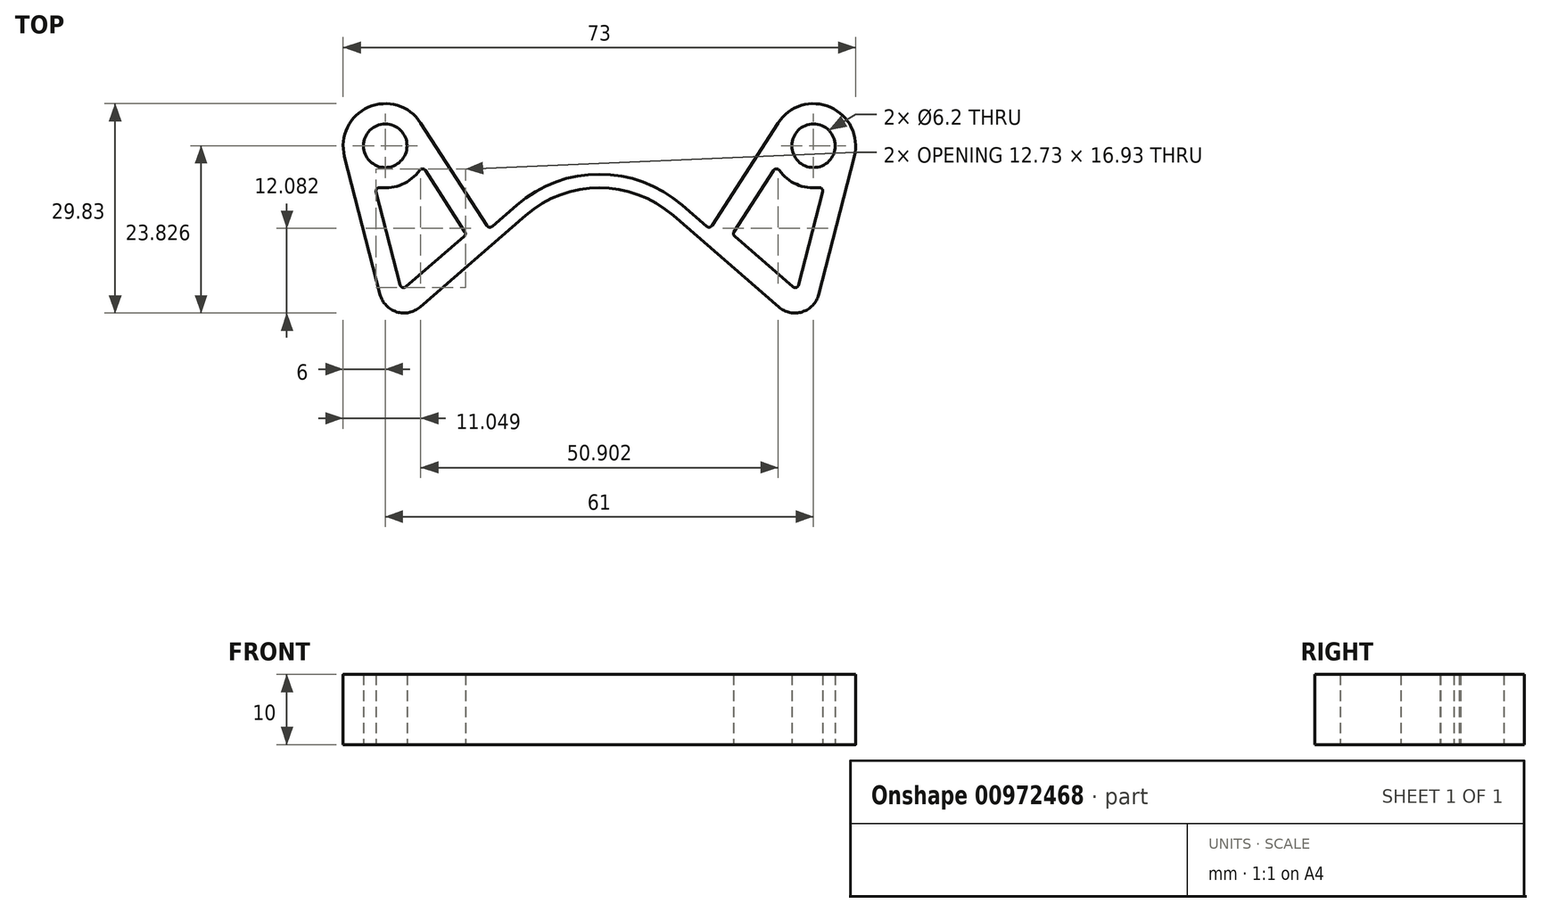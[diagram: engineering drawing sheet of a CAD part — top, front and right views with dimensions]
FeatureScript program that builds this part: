
annotation { "Feature Type Name" : "Feature", "Feature Type Description" : "" }
export const myFeature = defineFeature(function(context is Context, id is Id, definition is map)
    precondition{}
    {
        {
            var Q0;
            Q0=qCreatedBy(makeId("Top.planeOp"),FACE);
            var sketch = newSketch(context, id + "F0", { "sketchPlane" : qUnion([Q0])});
            skCircle(sketch, "E0", {"center": v(30.5, 20.33) * mm, "radius": 3.1 * mm});
            skArc(sketch, "E1", {"start": v(25.62, 16.84) * mm, "mid": v(28.1, 14.83) * mm, "end": v(31.25, 14.37) * mm});
            skArc(sketch, "E2", {"start": v(25.54, -2.64) * mm, "mid": v(28.88, -3.34) * mm, "end": v(31.23, -0.87) * mm});
            skLineSegment(sketch, "E3", {"start": v(31.23, -0.87) * mm, "end": v(36.3, 18.83) * mm});
            skArc(sketch, "E4", {"start": v(10.5, 10.41) * mm, "mid": v(5.6, 13.32) * mm, "end": v(0, 14.34) * mm});
            skLineSegment(sketch, "E5", {"start": v(10.5, 10.41) * mm, "end": v(25.54, -2.64) * mm});
            skArc(sketch, "E6", {"start": v(15.28, 8.85) * mm, "mid": v(15.68, 8.73) * mm, "end": v(16.03, 8.95) * mm});
            skLineSegment(sketch, "E7", {"start": v(16.03, 8.95) * mm, "end": v(25.46, 23.58) * mm});
            skLineSegment(sketch, "E8", {"start": v(19.17, 8.1) * mm, "end": v(24.79, 16.82) * mm});
            skLineSegment(sketch, "E9", {"start": v(19.26, 7.45) * mm, "end": v(27.57, 0.24) * mm});
            skLineSegment(sketch, "E10", {"start": v(31.8, 13.75) * mm, "end": v(28.38, 0.49) * mm});
            skArc(sketch, "E11.trimOffspring", {"start": v(36.3, 18.83) * mm, "mid": v(32.9, 25.82) * mm, "end": v(25.46, 23.58) * mm});
            skPoint(sketch, "E12.visualSharp", {"position": v(18.93, 7.73) * mm});
            skArc(sketch, "E12.filletArc", {"start": v(19.17, 8.1) * mm, "mid": v(19.1, 7.75) * mm, "end": v(19.26, 7.45) * mm});
            skPoint(sketch, "E13.visualSharp", {"position": v(25.22, 17.48) * mm});
            skArc(sketch, "E13.filletArc", {"start": v(25.62, 16.84) * mm, "mid": v(25.2, 17.05) * mm, "end": v(24.79, 16.82) * mm});
            skPoint(sketch, "E14.visualSharp", {"position": v(32, 14.52) * mm});
            skArc(sketch, "E14.filletArc", {"start": v(31.8, 13.75) * mm, "mid": v(31.7, 14.2) * mm, "end": v(31.25, 14.37) * mm});
            skPoint(sketch, "E15.visualSharp", {"position": v(28.18, -0.3) * mm});
            skArc(sketch, "E15.filletArc", {"start": v(27.57, 0.24) * mm, "mid": v(28.04, 0.14) * mm, "end": v(28.38, 0.49) * mm});
            skLineSegment(sketch, "E16", {"start": v(11.78, 11.89) * mm, "end": v(15.28, 8.85) * mm});
            skArc(sketch, "E17.trimOffspring", {"start": v(11.78, 11.89) * mm, "mid": v(6.29, 15.15) * mm, "end": v(0, 16.29) * mm});
            skArc(sketch, "E18.MirrorCS", {"start": v(-27.57, 0.24) * mm, "mid": v(-28.04, 0.14) * mm, "end": v(-28.38, 0.49) * mm});
            skArc(sketch, "E19.MirrorCS", {"start": v(-25.62, 16.84) * mm, "mid": v(-25.2, 17.05) * mm, "end": v(-24.79, 16.82) * mm});
            skArc(sketch, "E20.MirrorCS", {"start": v(-31.8, 13.75) * mm, "mid": v(-31.7, 14.2) * mm, "end": v(-31.25, 14.37) * mm});
            skArc(sketch, "E21.MirrorCS", {"start": v(-19.17, 8.1) * mm, "mid": v(-19.1, 7.75) * mm, "end": v(-19.26, 7.45) * mm});
            skArc(sketch, "E22.MirrorCS", {"start": v(-15.28, 8.85) * mm, "mid": v(-15.68, 8.73) * mm, "end": v(-16.03, 8.95) * mm});
            skPoint(sketch, "E23.MirrorP", {"position": v(-27.84, 0) * mm});
            skArc(sketch, "E24.MirrorCS", {"start": v(-10.5, 10.41) * mm, "mid": v(-5.6, 13.32) * mm, "end": v(0, 14.34) * mm});
            skPoint(sketch, "E25.MirrorP", {"position": v(-18.93, 7.73) * mm});
            skArc(sketch, "E26.MirrorCS", {"start": v(-25.54, -2.64) * mm, "mid": v(-28.88, -3.34) * mm, "end": v(-31.23, -0.87) * mm});
            skPoint(sketch, "E27.MirrorP", {"position": v(-28.18, -0.3) * mm});
            skLineSegment(sketch, "E28.MirrorCS", {"start": v(-16.03, 8.95) * mm, "end": v(-25.46, 23.58) * mm});
            skArc(sketch, "E29.MirrorCS", {"start": v(-25.62, 16.84) * mm, "mid": v(-28.1, 14.83) * mm, "end": v(-31.25, 14.37) * mm});
            skLineSegment(sketch, "E30.MirrorCS", {"start": v(-19.17, 8.1) * mm, "end": v(-24.79, 16.82) * mm});
            skLineSegment(sketch, "E31.MirrorCS", {"start": v(-11.78, 11.89) * mm, "end": v(-15.28, 8.85) * mm});
            skArc(sketch, "E32.MirrorCS", {"start": v(-36.3, 18.83) * mm, "mid": v(-32.9, 25.82) * mm, "end": v(-25.46, 23.58) * mm});
            skCircle(sketch, "E33.MirrorC", {"center": v(-30.5, 20.33) * mm, "radius": 3.1 * mm});
            skArc(sketch, "E34.MirrorCS", {"start": v(-11.78, 11.89) * mm, "mid": v(-6.29, 15.15) * mm, "end": v(0, 16.29) * mm});
            skLineSegment(sketch, "E35.MirrorCS", {"start": v(-31.8, 13.75) * mm, "end": v(-28.38, 0.49) * mm});
            skLineSegment(sketch, "E36.MirrorCS", {"start": v(-31.23, -0.87) * mm, "end": v(-36.3, 18.83) * mm});
            skPoint(sketch, "E37.MirrorP", {"position": v(-25.22, 17.48) * mm});
            skPoint(sketch, "E38.MirrorP", {"position": v(-32, 14.52) * mm});
            skLineSegment(sketch, "E39.MirrorCS", {"start": v(-10.5, 10.41) * mm, "end": v(-25.54, -2.64) * mm});
            skLineSegment(sketch, "E40.MirrorCS", {"start": v(-19.26, 7.45) * mm, "end": v(-27.57, 0.24) * mm});
            skSolve(sketch);
        }
        {
            var Q0;
            Q0=makeQuery(id+"F0.imprint","IMPRINT",FACE,{"disambiguationData":[TD([[makeQuery(id+"F0.imprint","IMPRINT",EDGE,{"derivedFrom":sQuery(id+"F0.wireOp",EDGE,"E0")}),-1.0]])]});
            extrude(context, id + "F1", {"entities" : qUnion([Q0]), "depth" : 10 * mm, "offsetDistance" : 25 * mm});
        }
    });
